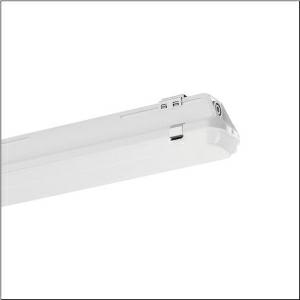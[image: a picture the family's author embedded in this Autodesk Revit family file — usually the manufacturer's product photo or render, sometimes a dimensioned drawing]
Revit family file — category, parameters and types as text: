
# Revit family: monsun_r__21_51fb10dl440k_c082
name_source: partatom
category: Lighting Fixtures
units: mm (PartAtom-declared; Revit-internal decimal feet)

## family parameters
Cut with Voids When Loaded = No
Host = Face
Light Source = No
Part Type = Normal
Room Calculation Point = No
Round Connector Dimension = Use Diameter
Shared = No

## types (1)
- --- (1 x LED, 4330 lm, 24.3 W, 4000K)
    Apparent Load = 24 VA
    CIE Flux Codes = 46 76 93 94 100
    Color Rendering = 80
    Color Temperature = 4000K
    Default Elevation = 1800 mm
    Description = Monsun® 21, damp-proof luminaire, chain hanger, primary optical cover: enclosure, of PMMA, light emission: direct distribution, primary light characteristic: symmetric, installation type: suspended mounting, surface-mounted, horizontal mounting, vertical mounting, LED, rated luminous flux: 4.330lm, luminous efficacy: 178lm/W, light colour: 840, colour temperature: 4000K, control gear: DALI 2, with terminal, 5-pole, max. 2.5mm², mains connection: 220..240V, AC, 50/60Hz, rated input power: 25W, housing, of glass-fibre reinforced plastic, uncoated, bright grey, incl. chain hanger, length: 1.299mm, width: 90mm, height: 88mm, clip for enclosure, of stainless steel (V2A), ceiling mounting element, of stainless steel (V2A), chain hanger, of stainless steel (V2A), protection rating (complete): IP66, insulation class (complete): insulation class I (protective earthing), certification: CE, ENEC, VDE, UKCA, protection symbol: D, impact resistance: IK04, permissible operating ambient temperature: -25..+35°C, standard: EN 50419, EN 60598-2-1, corresponds to IFS (International Featured Standards) requirements for safety and quality in the food industry, for indoor or canopied outdoor use, no direct snow, no direct sun, no direct rain, LABS conformity tested according to VDMA 24364:2018-05, contact your sales advisor before using the luminaires in applications with unclear chemical exposure, large temperature fluctuations or condensation-forming humidity, packaging unit: 1 piece
    Height = 88 mm
    Lamp = 1 x LED
    Lamp Light Flux = 4330 lm
    Lamp Power = 24.3 W
    Lamp count = 1
    Length = 1299 mm
    Luminous efficacy = 178 lm/W
    Manufacturer = Siteco
    ModVariant = No
    Model = 51FB10DL440K
    Mounting Place = Ceiling
    Mounting Type = Surface mounted
    Number of Poles = 1
    OnlyDefault = Yes
    Power Factor = 1
    Product Name = Monsun® 21
    Product group = damp-proof luminaire
    ProductGroupID = 300
    Protection Class = Protection class I
    Protection Degree = IP 66
    RLX_Detail_Level = 1
    RLX_Emergency_Light_Flux = 0 lm
    RLX_Emergency_Type = 0
    RLX_Emergency_Type_DB = No
    RlxData = <blob elided: 93453 chars, md5=babc1301>
    Socket = socket
    Standby Power = 0 W
    System Light Flux = 4330 lm
    System Power = 24 W
    Type Comments = factory setting: luminous flux: 100 % | dim-lin: 254 | 164 mA
    Type Image = l_1319656.jpg
    URL = http://relux.com
    VarID = @adj_022492
    Voltage = 0 V
    Weight = 0.00 kg
    Width = 90 mm

## geometry (parser evidence)
native form markers: Blend x4, Sweep x11
no freeform markers — native parametric forms only
